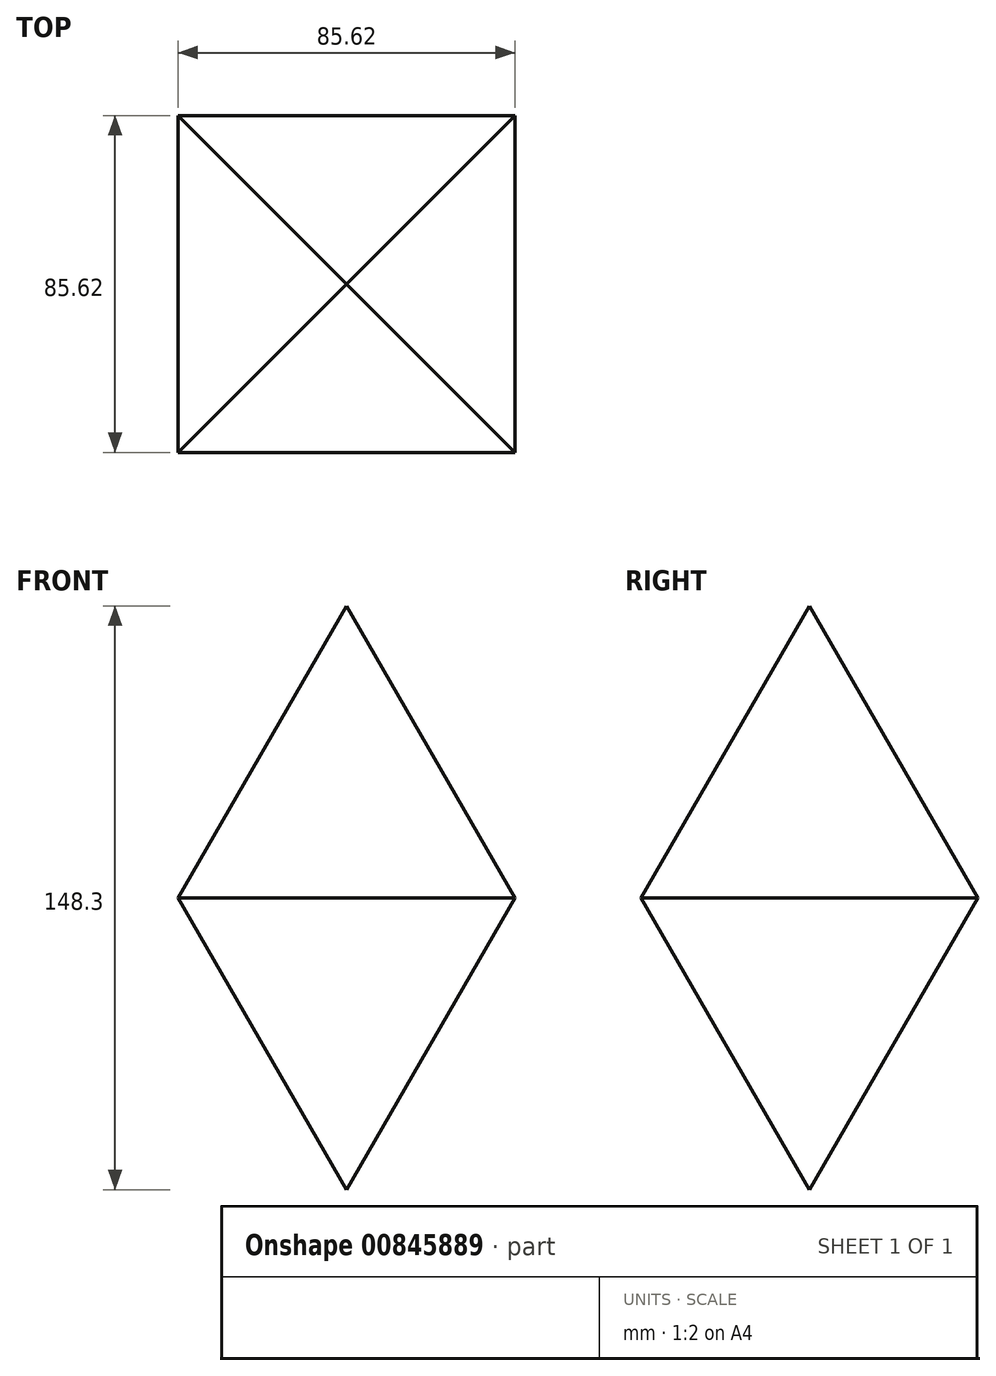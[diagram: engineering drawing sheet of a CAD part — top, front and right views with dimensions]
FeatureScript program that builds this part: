
annotation { "Feature Type Name" : "Feature", "Feature Type Description" : "" }
export const myFeature = defineFeature(function(context is Context, id is Id, definition is map)
    precondition{}
    {
        {
            var Q0;
            Q0=qCreatedBy(makeId("Top.planeOp"),FACE);
            var sketch = newSketch(context, id + "F0", { "sketchPlane" : qUnion([Q0])});
            skLineSegment(sketch, "E0.bottom", {"start": v(42.8, 42.8) * mm, "end": v(-42.8, 42.8) * mm});
            skLineSegment(sketch, "E0.top", {"start": v(42.8, -42.8) * mm, "end": v(-42.8, -42.8) * mm});
            skLineSegment(sketch, "E0.left", {"start": v(42.8, 42.8) * mm, "end": v(42.8, -42.8) * mm});
            skLineSegment(sketch, "E0.right", {"start": v(-42.8, 42.8) * mm, "end": v(-42.8, -42.8) * mm});
            skPoint(sketch, "E0.middle", {"position": v(0, 0) * mm});
            skSolve(sketch);
        }
        {
            var Q0;
            Q0=makeQuery(id+"F0.imprint","IMPRINT",FACE,{"disambiguationData":[TD([[makeQuery(id+"F0.imprint","IMPRINT",EDGE,{"derivedFrom":sQuery(id+"F0.wireOp",EDGE,"E0.bottom")}),1.0]])]});
            extrude(context, id + "F1", {"entities" : qUnion([Q0]), "depth" : 105.92 * mm, "offsetDistance" : 25.4 * mm, "hasDraft" : true, "draftAngle" : 30 * degree, "draftPullDirection" : true, "hasSecondDirection" : true, "secondDirectionOppositeDirection" : true, "secondDirectionDepth" : 762 * mm, "hasSecondDirectionDraft" : true, "secondDirectionDraftAngle" : 30 * degree, "secondDirectionDraftPullDirection" : true});
        }
    });
